# Revit family: Saxi Varioplan 40S
name_source: partatom
category: Specialty Equipment
revit_build: Autodesk Revit Architecture 2015 (Build: 20140322_1515(x64)
units: mm (PartAtom-declared; Revit-internal decimal feet)

## types (1)
- Saxi Varioplan 40S
    Actual_No_Panels = 5
    Actual_Panel_Width = 627 mm
    CentrumToPanel_Inkörd = 304 mm
    Even_Panels = Yes
    First_helpanel = 70 mm  [stored 0.229659 ft]
    Height = 2700 mm  [stored 8.85827 ft]
    Karm1 = 75 mm
    Karm2 = 75 mm
    KarmHeight = 2590 mm
    Manufacturer = Saxi Vägg AB
    Model = Varioplan 40S
    No_Panels = 4
    Panel_Offsets = 627 mm
    Skivbredd = 607 mm
    Skivbredd_Halvpanel = 269 mm
    Skivhöjd = 2550 mm
    TMP1 = 2
    TMP2 = 2
    TMP3 = 0
    To_Halfpanel = 75 mm
    URL = http://www.saxi.se
    Wanted_Panel_Width = 700 mm  [stored 2.29659 ft]
    Width = 3560 mm  [stored 11.6798 ft]

note: [stored X ft] marks values corroborated as IEEE doubles in the binary element streams (Revit-internal decimal feet)

## geometry (parser evidence)
native form markers: Sweep x18
no freeform markers — native parametric forms only
